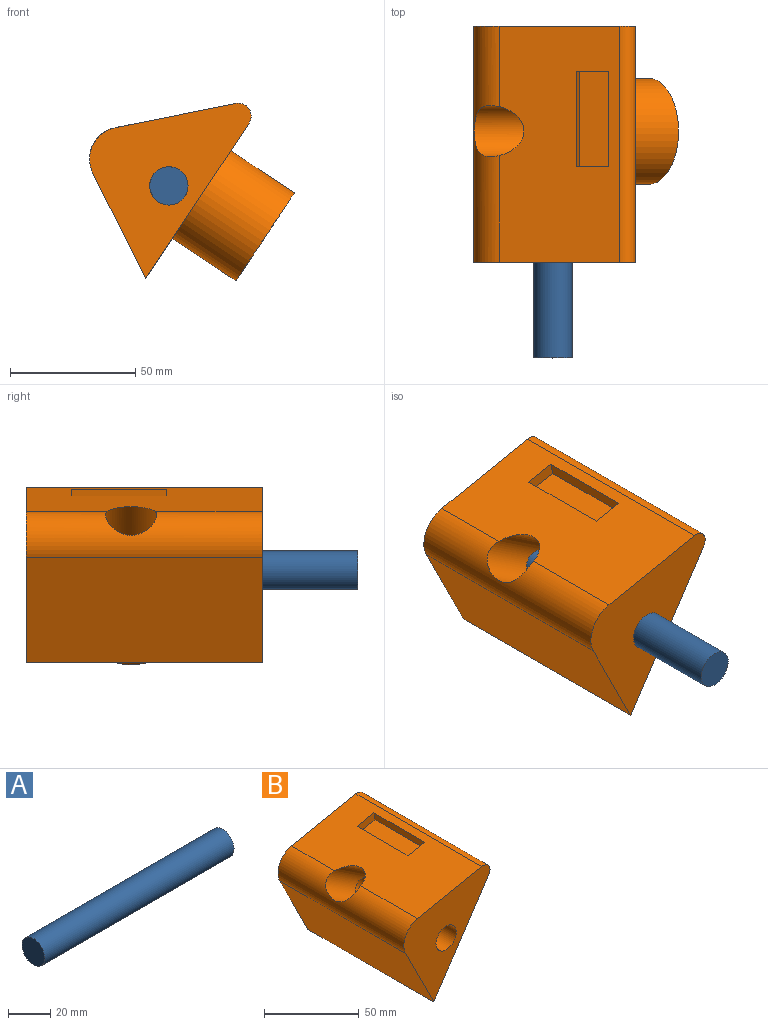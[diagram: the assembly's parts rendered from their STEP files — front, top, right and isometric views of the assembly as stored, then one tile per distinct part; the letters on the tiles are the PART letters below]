
ASSEMBLY  parts=2 mates=1
PART A: 3 faces, bbox 127x15.2x15.2 mm
  f0: cylinder r=7.62mm len=127mm, axis (-1,0,0), area 6080.5mm2, adj f1,f2
  f1: plane 15.24x15.24mm, normal (1,0,0), area 182.4mm2, adj f0
  f2: plane 15.24x15.24mm, normal (-1,0,0), area 182.4mm2, adj f0
PART B: 16 faces, bbox 81.9x94.1x70.8 mm
  f0: plane 94.14x48.12mm, normal (-0.2,0,0.98), area 3992.7mm2, adj f3,f4,f7,f8,f9,f10,f11,f13
  f1: plane 94.14x61.92mm, normal (0.83,0,-0.55), area 5612.4mm2, adj f2,f3,f4,f5,f13
  f2: plane 94.14x41.9mm, normal (-0.89,0,-0.45), area 4412.3mm2, adj f1,f3,f4,f14
  f3: plane 69.81x64.4mm, normal (0,-1,0), area 2111.1mm2, adj f0,f1,f2,f13,f14,f15
  f4: plane 69.81x64.4mm, normal (0,1,0), area 2111.1mm2, adj f0,f1,f2,f13,f14,f15
  f5: cylinder r=21.03mm len=51.92mm, axis (-0.83,0,0.55), area 4031.9mm2, adj f1,f6
  f6: plane 42.05x35.01mm, normal (0.83,0,-0.55), area 1062mm2, adj f5,f7
  f7: cylinder r=10.2mm len=75.93mm, axis (0.83,0,-0.55), area 4253.8mm2, adj f0,f6,f14,f15
  f8: plane 38.1x4.98mm, normal (0.98,0,0.2), area 193.5mm2, adj f0,f9,f11,f12
  f9: plane 13.45x7.48mm, normal (0,1,0), area 64.5mm2, adj f0,f8,f10,f12
  f10: plane 38.1x4.98mm, normal (-0.98,0,-0.2), area 193.5mm2, adj f0,f9,f11,f12
  f11: plane 13.45x7.48mm, normal (0,-1,0), area 64.5mm2, adj f0,f8,f10,f12
  f12: plane 38.1x12.45mm, normal (-0.2,0,0.98), area 483.9mm2, adj f8,f9,f10,f11
  f13: cylinder r=5.08mm len=94.14mm, axis (0,-1,0), area 1126.8mm2, adj f0,f1,f3,f4
  f14: cylinder r=12.7mm len=94.14mm, axis (0,-1,0), area 1951.3mm2, adj f0,f2,f3,f4,f7
  f15: cylinder r=7.62mm len=94.14mm, axis (0,-1,0), area 3865.2mm2, adj f3,f4,f7
PLACE A rot(axis=(-0.58,-0.58,0.58),120deg) t=(-53.99,-137.69,7.31)mm
PLACE B rot(axis=(-0.69,0.19,-0.7),0deg) t=(-63.25,-5.44,-9.29)mm
MATE fastened A.f0 <-> B.f15  axis (0,-1,0) through (-53.99,-74.19,7.31)mm
